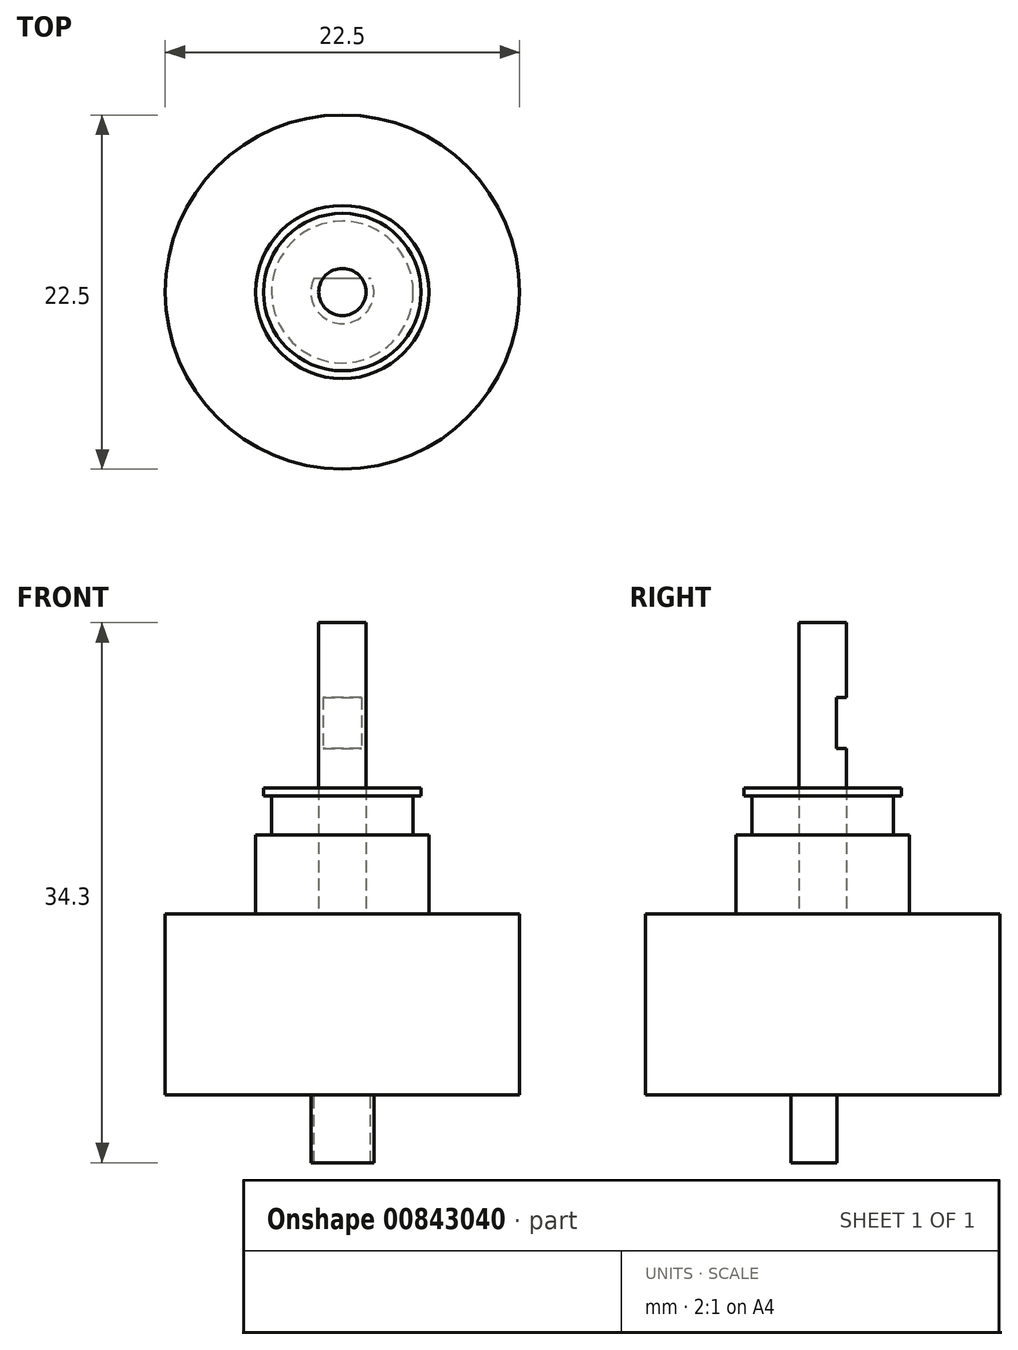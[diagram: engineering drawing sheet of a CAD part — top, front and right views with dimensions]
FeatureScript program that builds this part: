
annotation { "Feature Type Name" : "Feature", "Feature Type Description" : "" }
export const myFeature = defineFeature(function(context is Context, id is Id, definition is map)
    precondition{}
    {
        {
            var Q0;
            Q0=qCreatedBy(makeId("Top.planeOp"),FACE);
            var sketch = newSketch(context, id + "F0", { "sketchPlane" : qUnion([Q0])});
            skCircle(sketch, "E0", {"center": v(0, 0) * mm, "radius": 11.25 * mm});
            skCircle(sketch, "E1", {"center": v(0, 0) * mm, "radius": 1.5 * mm});
            skLineSegment(sketch, "E2", {"start": v(-1.21, 0.88) * mm, "end": v(1.21, 0.88) * mm});
            skSolve(sketch);
        }
        {
            var Q0;
            Q0=makeQuery(id+"F0.imprint","IMPRINT",FACE,{"disambiguationData":[TD([[makeQuery(id+"F0.imprint","IMPRINT",EDGE,{"derivedFrom":sQuery(id+"F0.wireOp",EDGE,"E0")}),1.0]])]});
            var Q1;
            Q1=makeQuery(id+"F0.imprint","IMPRINT",FACE,{"disambiguationData":[TD([[makeQuery(id+"F0.imprint","IMPRINT",EDGE,{"derivedFrom":sQuery(id+"F0.wireOp",EDGE,"E1")}),-1.0]])]});
            extrude(context, id + "F1", {"entities" : qUnion([Q0, Q1]), "depth" : 11.5 * mm, "offsetDistance" : 25 * mm});
        }
        {
            var Q0;
            Q0=makeQuery(id+"F0.imprint","IMPRINT",FACE,{"disambiguationData":[TD([[makeQuery(id+"F0.imprint","IMPRINT",EDGE,{"derivedFrom":sQuery(id+"F0.wireOp",EDGE,"E1")}),1.0]])]});
            extrude(context, id + "F2", {"entities" : qUnion([Q0]), "operationType" : NewBodyOperationType.ADD, "depth" : 30 * mm, "offsetDistance" : 25 * mm});
        }
        {
            var Q0;
            {var subQ0=sQuery(id+"F0.wireOp",EDGE,"E2");Q0=makeQuery(id+"F0.imprint","IMPRINT",FACE,{"disambiguationData":[TD([[makeQuery(id+"F0.imprint","IMPRINT",EDGE,{"derivedFrom":subQ0}),1.0]])]});}
            extrude(context, id + "F3", {"entities" : qUnion([Q0]), "operationType" : NewBodyOperationType.REMOVE, "depth" : 25.25 * mm, "offsetDistance" : 25 * mm, "hasSecondDirection" : true, "secondDirectionOppositeDirection" : false, "secondDirectionDepth" : 22 * mm});
        }
        {
            var Q0;
            Q0=makeQuery(id+"F1.opExtrude","CAP_FACE",FACE,{"disambiguationData":[OSD([sQuery(id+"F0.wireOp",EDGE,"E0"),sQuery(id+"F0.wireOp",EDGE,"E1")])],"isStart":false});
            var sketch = newSketch(context, id + "F4", { "sketchPlane" : qUnion([Q0])});
            skCircle(sketch, "E3", {"center": v(0, 0) * mm, "radius": 4.5 * mm});
            skCircle(sketch, "E4", {"center": v(0, 0) * mm, "radius": 5 * mm});
            skCircle(sketch, "E5", {"center": v(0, 0) * mm, "radius": 5.5 * mm});
            skSolve(sketch);
        }
        {
            var Q0;
            Q0=makeQuery(id+"F4.imprint","IMPRINT",FACE,{"disambiguationData":[TD([[makeQuery(id+"F4.imprint","IMPRINT",EDGE,{"derivedFrom":sQuery(id+"F4.wireOp",EDGE,"E3")}),1.0]])]});
            var Q1;
            Q1=makeQuery(id+"F4.imprint","IMPRINT",FACE,{"disambiguationData":[TD([[makeQuery(id+"F4.imprint","IMPRINT",EDGE,{"derivedFrom":sQuery(id+"F4.wireOp",EDGE,"E3")}),-1.0]])]});
            var Q2;
            Q2=makeQuery(id+"F4.imprint","IMPRINT",FACE,{"disambiguationData":[TD([[makeQuery(id+"F4.imprint","IMPRINT",EDGE,{"derivedFrom":sQuery(id+"F4.wireOp",EDGE,"E4")}),-1.0]])]});
            extrude(context, id + "F5", {"entities" : qUnion([Q0, Q1, Q2]), "depth" : 8 * mm, "offsetDistance" : 25 * mm});
        }
        {
            var Q0;
            Q0=makeQuery(id+"F4.imprint","IMPRINT",FACE,{"disambiguationData":[TD([[makeQuery(id+"F4.imprint","IMPRINT",EDGE,{"derivedFrom":sQuery(id+"F4.wireOp",EDGE,"E4")}),-1.0]])]});
            extrude(context, id + "F6", {"entities" : qUnion([Q0]), "operationType" : NewBodyOperationType.REMOVE, "depth" : 8 * mm, "offsetDistance" : 25 * mm, "hasSecondDirection" : true, "secondDirectionOppositeDirection" : false, "secondDirectionDepth" : 5 * mm});
        }
        {
            var Q0;
            Q0=makeQuery(id+"F4.imprint","IMPRINT",FACE,{"disambiguationData":[TD([[makeQuery(id+"F4.imprint","IMPRINT",EDGE,{"derivedFrom":sQuery(id+"F4.wireOp",EDGE,"E3")}),-1.0]])]});
            extrude(context, id + "F7", {"entities" : qUnion([Q0]), "operationType" : NewBodyOperationType.REMOVE, "depth" : 7.5 * mm, "offsetDistance" : 25 * mm, "hasSecondDirection" : true, "secondDirectionOppositeDirection" : false, "secondDirectionDepth" : 5 * mm});
        }
        {
            var Q0;
            {var subQ0=sQuery(id+"F0.wireOp",EDGE,"E1");Q0=makeQuery(id+"F2.boolean.opBoolean","MERGE",FACE,{"derivedFrom":[makeQuery(id+"F1.opExtrude","CAP_FACE",FACE,{"disambiguationData":[OSD([sQuery(id+"F0.wireOp",EDGE,"E0"),subQ0])],"isStart":true}),makeQuery(id+"F2.opExtrude","CAP_FACE",FACE,{"disambiguationData":[OSD([subQ0])],"isStart":true})]});}
            var sketch = newSketch(context, id + "F8", { "sketchPlane" : qUnion([Q0])});
            skCircle(sketch, "E6", {"center": v(0, 0) * mm, "radius": 2 * mm});
            skLineSegment(sketch, "E7", {"start": v(-1.79, -0.9) * mm, "end": v(1.79, -0.9) * mm});
            skSolve(sketch);
        }
        {
            var Q0;
            {var subQ0=sQuery(id+"F8.wireOp",EDGE,"E7");Q0=makeQuery(id+"F8.imprint","IMPRINT",FACE,{"disambiguationData":[TD([[makeQuery(id+"F8.imprint","IMPRINT",EDGE,{"derivedFrom":subQ0}),1.0]])]});}
            extrude(context, id + "F9", {"entities" : qUnion([Q0]), "operationType" : NewBodyOperationType.ADD, "depth" : 4.3 * mm, "offsetDistance" : 25 * mm});
        }
    });
